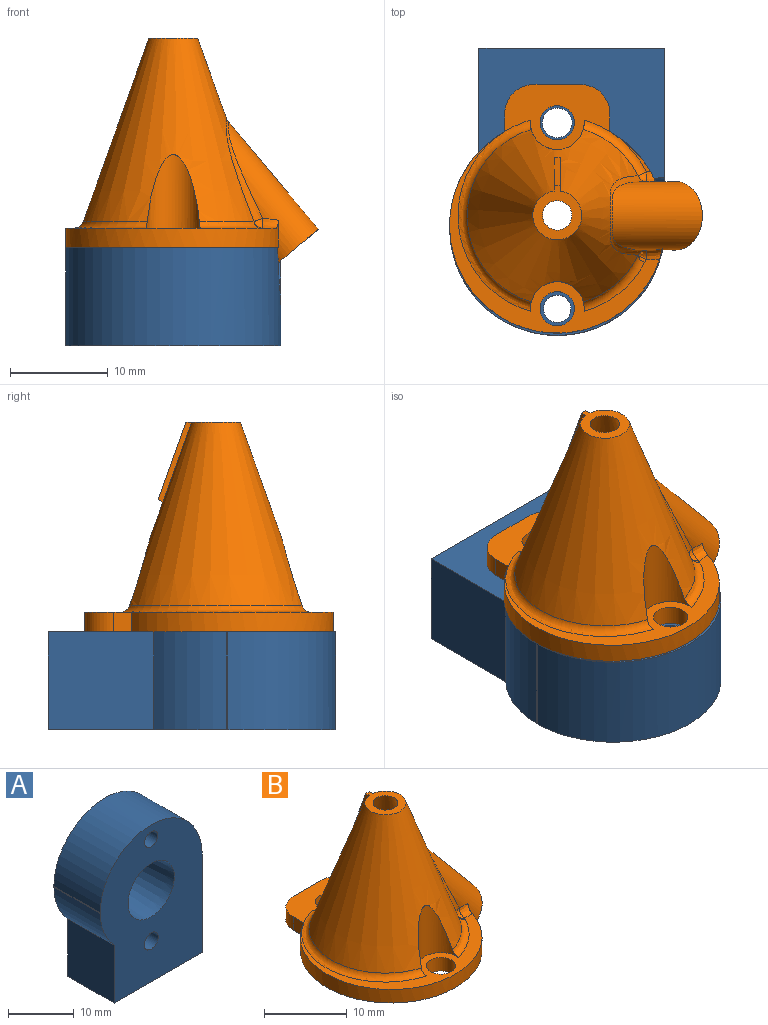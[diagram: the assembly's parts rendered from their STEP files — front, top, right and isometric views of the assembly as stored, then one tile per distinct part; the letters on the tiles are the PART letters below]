
ASSEMBLY  parts=2 mates=1
PART A: 17 faces, bbox 25.1x11.8x29.3 mm
  f0: plane 19x10mm, normal (0,0,-1), area 179.4mm2, adj f2,f3,f4,f7,f9,f13
  f1: plane 10x0.13mm, normal (-1,0,0), area 1.3mm2, adj f2,f3,f5,f14
  f2: plane 29.33x22mm, normal (0,1,0), area 462.5mm2, adj f0,f1,f4,f5,f6,f11,f12,f13
  f3: plane 29.33x22mm, normal (0,-1,0), area 461.9mm2, adj f0,f1,f4,f5,f6,f11,f12,f13
  f4: plane 18.33x10mm, normal (1,0,0), area 153.2mm2, adj f0,f2,f3,f5,f16
  f5: cylinder r=11mm len=22mm, axis (0,-1,0), area 333.1mm2, adj f1,f2,f3,f4,f16
  f6: cone r=5mm half-angle=5deg, axis (0,-1,0), area 287.8mm2, adj f2,f3
  f7: cylinder r=1.3mm len=10mm, axis (0,0,-1), area 81.7mm2, adj f0,f8
  f8: plane 2.6x2.6mm, normal (0,0,-1), area 5.3mm2, adj f7
  f9: cylinder r=1.3mm len=10mm, axis (0,0,-1), area 81.7mm2, adj f0,f10
  f10: plane 2.6x2.6mm, normal (0,0,-1), area 5.3mm2, adj f9
  f11: cylinder r=1.52mm len=10mm, axis (0,-1,0), area 95.4mm2, adj f2,f3
  f12: cylinder r=1.4mm len=10mm, axis (0,-1,0), area 88mm2, adj f2,f3
  f13: plane 10.78x10mm, normal (-1,0,0), area 107.8mm2, adj f0,f2,f3,f15
  f14: plane 10x0mm, normal (0,0,-1), area 0mm2, adj f1,f2,f3,f15
  f15: cylinder r=11mm len=10mm, axis (0,-1,0), area 81.9mm2, adj f2,f3,f13,f14
  f16: cylinder r=4mm len=8.87mm, axis (-0.5,0.87,0), area 59.7mm2, adj f2,f4,f5
PART B: 52 faces, bbox 28.3x27.1x25.7 mm
  f0: cylinder r=1.75mm len=3.5mm, axis (0,0,1), area 22mm2, adj f7,f19
  f1: cylinder r=1.75mm len=3.5mm, axis (0,0,1), area 22mm2, adj f6,f19
  f2: cone r=9.44mm half-angle=19.7deg, axis (0,0,-1), area 590.7mm2, adj f3,f4,f5,f21,f38,f43,f44,f46
  f3: torus R=10.15mm, axis (0,0,1), area 9.7mm2, adj f2,f6,f11,f14,f20,f39,f44
  f4: torus R=10.15mm, axis (0,0,1), area 9.8mm2, adj f2,f7,f41,f43
  f5: torus R=10.15mm, axis (0,0,1), area 30.3mm2, adj f2,f6,f7,f12,f13,f43,f44
  f6: plane 10.76x6.66mm, normal (0,0,1), area 41.7mm2, adj f1,f3,f5,f12,f14,f15,f16,f17
  f7: plane 21.45x20.59mm, normal (0,0,1), area 54.5mm2, adj f0,f4,f5,f13,f42,f43
  f8: plane 9.4x2.31mm, normal (0,0,1), area 8.7mm2, adj f10,f18,f27,f33
  f9: plane 11.11x5.15mm, normal (0,0,1), area 11.9mm2, adj f10,f18,f22,f23,f26,f32,f49
  f10: cone r=7.44mm half-angle=17deg, axis (0,0,-1), area 378.4mm2, adj f8,f9,f21,f26,f27,f28,f29,f32
  f11: cylinder r=11mm len=5.35mm, axis (0,0,1), area 14.5mm2, adj f3,f14,f19,f20,f24,f40
  f12: plane 2x1.81mm, normal (-1,0,0), area 3.6mm2, adj f5,f6,f13,f17,f19
  f13: cylinder r=11mm len=21.74mm, axis (0,0,1), area 87.6mm2, adj f5,f7,f12,f19,f24,f42
  f14: plane 2x1.81mm, normal (1,0,0), area 3.6mm2, adj f3,f6,f11,f15,f19
  f15: cylinder r=3mm len=3mm, axis (0,0,1), area 9.4mm2, adj f6,f14,f16,f19
  f16: plane 4.76x2mm, normal (0,1,0), area 9.5mm2, adj f6,f15,f17,f19
  f17: cylinder r=3mm len=3mm, axis (0,0,1), area 9.4mm2, adj f6,f12,f16,f19
  f18: cylinder r=6.5mm len=13mm, axis (0,0,1), area 79.8mm2, adj f8,f9,f19,f22,f31,f34
  f19: plane 25.4x21.74mm, normal (0,0,-1), area 248.2mm2, adj f0,f1,f11,f12,f13,f14,f15,f16
  f20: plane 4.14x4.1mm, normal (0,0,1), area 1mm2, adj f3,f11,f40
  f21: plane 5.57x5mm, normal (0,0,1), area 12.9mm2, adj f2,f10,f45,f47,f48
  f22: cylinder r=3.5mm len=3.57mm, axis (-0.64,0,0.77), area 1.8mm2, adj f9,f18
  f23: cylinder r=2.25mm len=14.29mm, axis (-0.64,0,0.77), area 110mm2, adj f9,f25,f49
  f24: cylinder r=3.5mm len=15.48mm, axis (-0.64,0,0.77), area 155.9mm2, adj f11,f13,f19,f25,f38,f40,f42
  f25: plane 7x5.36mm, normal (0.64,0,-0.77), area 22.6mm2, adj f23,f24
  f26: cylinder r=1.5mm len=5.35mm, axis (0,0,-1), area 4.7mm2, adj f9,f10,f28,f31
  f27: cylinder r=1.5mm len=5.35mm, axis (0,0,-1), area 4.8mm2, adj f8,f10,f29,f31
  f28: plane 5.45x1.21mm, normal (0,-1,0), area 5.5mm2, adj f10,f26,f30,f31,f51
  f29: plane 5.45x1.21mm, normal (0,-1,0), area 5.5mm2, adj f10,f27,f30,f31,f51
  f30: cylinder r=5mm len=6.52mm, axis (0,0,-1), area 30.5mm2, adj f28,f29,f31,f51
  f31: plane 10.26x2.71mm, normal (0,0,-1), area 14.5mm2, adj f18,f26,f27,f28,f29,f30
  f32: cylinder r=1.5mm len=5.35mm, axis (0,0,-1), area 4.7mm2, adj f9,f10,f34,f35
  f33: cylinder r=1.5mm len=5.35mm, axis (0,0,-1), area 4.7mm2, adj f8,f10,f34,f37
  f34: plane 10.26x2.71mm, normal (0,0,-1), area 14.5mm2, adj f18,f32,f33,f35,f36,f37
  f35: plane 5.45x1.21mm, normal (0,1,0), area 5.5mm2, adj f10,f32,f34,f36,f50
  f36: cylinder r=5mm len=6.52mm, axis (0,0,-1), area 30.5mm2, adj f34,f35,f37,f50
  f37: plane 5.45x1.21mm, normal (0,1,0), area 5.5mm2, adj f10,f33,f34,f36,f50
  f38: bspline ~12.75x8.17mm, area 16.9mm2, adj f2,f24,f39,f41
  f39: sphere r=1mm, area 1mm2, adj f3,f38,f40
  f40: bspline ~1.07x1.03mm, area 1.1mm2, adj f11,f20,f24,f39
  f41: sphere r=1mm, area 0.8mm2, adj f4,f38,f42
  f42: bspline ~1.86x1.13mm, area 2.2mm2, adj f7,f13,f24,f41
  f43: cylinder r=2.75mm len=7.52mm, axis (0,0,-1), area 36.5mm2, adj f2,f4,f5,f7
  f44: cylinder r=2.75mm len=7.52mm, axis (0,0,-1), area 36.5mm2, adj f2,f3,f5,f6
  f45: plane 7.93x2.83mm, normal (0,0.94,0.34), area 5.1mm2, adj f21,f46,f47,f48
  f46: plane 0.61x0.51mm, normal (0,0.34,-0.94), area 0.3mm2, adj f2,f45,f47,f48
  f47: plane 8.2x3.51mm, normal (1,0,0), area 4.6mm2, adj f2,f21,f45,f46
  f48: plane 8.2x3.51mm, normal (-1,0,0), area 4.6mm2, adj f2,f21,f45,f46
  f49: bspline ~12.38x5.63mm, area 24.1mm2, adj f9,f10,f23
  f50: cone r=5.8mm half-angle=36.5deg, axis (0,0,1), area 11.4mm2, adj f10,f35,f36,f37
  f51: cone r=5.8mm half-angle=36.5deg, axis (0,0,1), area 11.4mm2, adj f10,f28,f29,f30
PLACE A rot(axis=(1,0,0),90deg) t=(19.25,11.96,-16.4)mm
PLACE B t=(8.25,-5.14,-4.4)mm
MATE fastened B.f1 <-> A.f11  axis (0,0,-1) through (8.25,4.36,-6.4)mm
